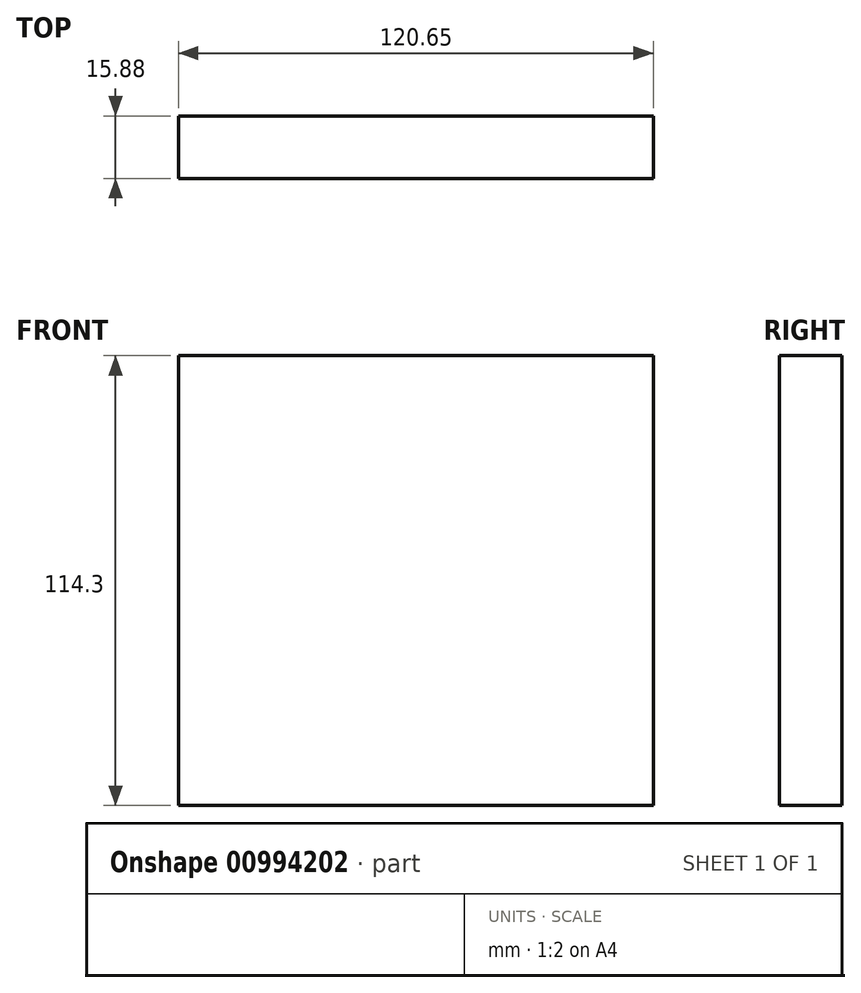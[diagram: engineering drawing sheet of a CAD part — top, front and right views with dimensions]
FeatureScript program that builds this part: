
annotation { "Feature Type Name" : "Feature", "Feature Type Description" : "" }
export const myFeature = defineFeature(function(context is Context, id is Id, definition is map)
    precondition{}
    {
        {
            var Q0;
            Q0=qCreatedBy(makeId("Front.planeOp"),FACE);
            var sketch = newSketch(context, id + "F0", { "sketchPlane" : qUnion([Q0])});
            skLineSegment(sketch, "E0.bottom", {"start": v(0, 0) * mm, "end": v(120.65, 0) * mm});
            skLineSegment(sketch, "E0.top", {"start": v(0, 114.3) * mm, "end": v(120.65, 114.3) * mm});
            skLineSegment(sketch, "E0.left", {"start": v(0, 0) * mm, "end": v(0, 114.3) * mm});
            skLineSegment(sketch, "E0.right", {"start": v(120.65, 0) * mm, "end": v(120.65, 114.3) * mm});
            skSolve(sketch);
        }
        {
            var Q0;
            Q0 = qSketchRegion(id + "F0", true);
            extrude(context, id + "F1", {"entities" : qUnion([Q0]), "depth" : 15.88 * mm, "offsetDistance" : 25.4 * mm});
        }
    });
